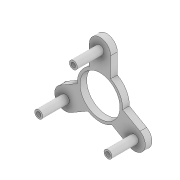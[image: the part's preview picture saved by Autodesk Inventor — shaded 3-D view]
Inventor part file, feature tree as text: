
AUTODESK INVENTOR PART (.ipt)
format: ipt  version: 2020.3 (Build 243373010, 373A)  size: 144,384 bytes
history: native  units: mm
features: sketch x4, extrude x2, pattern_circular x1, hole x1
ambient origin geometry x8: Origin, YZ Plane, XZ Plane, XY Plane, X Axis, Y Axis, Z Axis, Center Point
bodies: Body1 (feature_tree)
feature tree (8):
  extrude  "Extrusion3"  Depth=8.0mm
  extrude  "Extrusion4"  Depth=2.5mm TaperAngle=0.0deg
  sketch  "Sketch5"  dims[d20=3.0mm]
  pattern_circular  "Circular Pattern1"  [2 undecoded]
  hole  "Hole1"  [1 undecoded]
  sketch  "Sketch3"  dims[d13=15.0mm d14=8.0mm]
  sketch  "Sketch4"  dims[d17=15.0mm d18=2.5mm d19=0.0mm]
  sketch  "Sketch6"  dims[d21=10.0mm d22=0.0mm d23=15.0mm d26=17.0mm d27=30.0mm d29=360.0deg d31=30.0mm d32=360.0deg d34=1.729367mm d35=4.0mm d36=4.0mm d37=2.0mm d38=90.0deg d39=10.0mm d40=20.594885mm]
note: 3 required parameter values undecoded (feature->parameter linkage not recoverable at this tier; creation-order binding heuristic only, values carry confidence <= 0.55)
